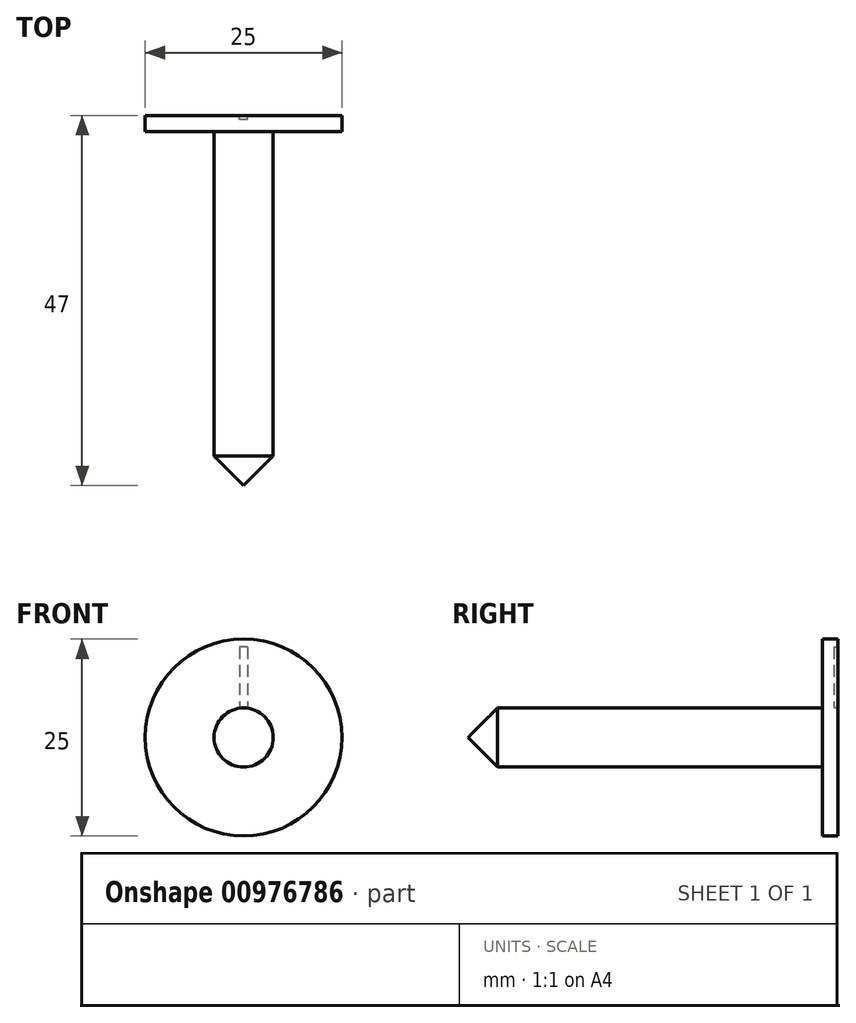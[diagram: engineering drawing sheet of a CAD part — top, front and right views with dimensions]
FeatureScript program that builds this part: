
annotation { "Feature Type Name" : "Feature", "Feature Type Description" : "" }
export const myFeature = defineFeature(function(context is Context, id is Id, definition is map)
    precondition{}
    {
        {
            var Q0;
            Q0=qCreatedBy(makeId("Front.planeOp"),FACE);
            var sketch = newSketch(context, id + "F0", { "sketchPlane" : qUnion([Q0])});
            skCircle(sketch, "E0", {"center": v(0, 0) * mm, "radius": 12.5 * mm});
            skSolve(sketch);
        }
        {
            var Q0;
            Q0 = qSketchRegion(id + "F0", true);
            extrude(context, id + "F1", {"entities" : qUnion([Q0]), "depth" : 2 * mm, "offsetDistance" : 25 * mm});
        }
        {
            var Q0;
            Q0=makeQuery(id+"F1.opExtrude","CAP_FACE",FACE,{"disambiguationData":[OSD([sQuery(id+"F0.wireOp",EDGE,"E0")])],"isStart":false});
            var sketch = newSketch(context, id + "F2", { "sketchPlane" : qUnion([Q0])});
            skCircle(sketch, "E1", {"center": v(0, 0) * mm, "radius": 3.75 * mm});
            skSolve(sketch);
        }
        {
            var Q0;
            Q0 = qSketchRegion(id + "F2", true);
            extrude(context, id + "F3", {"entities" : qUnion([Q0]), "operationType" : NewBodyOperationType.ADD, "depth" : 45 * mm, "offsetDistance" : 25 * mm});
        }
        {
            var Q0;
            Q0=makeQuery(id+"F3.opExtrude","CAP_EDGE",EDGE,{"disambiguationData":[OSD([sQuery(id+"F2.wireOp",EDGE,"E1")])],"isStart":false});
            chamfer(context, id + "F4", {"entities" : qUnion([Q0]), "width" : 3.75 * mm, "tangentPropagation" : true});
        }
        {
            var Q0;
            Q0=qCreatedBy(makeId("Right.planeOp"),FACE);
            var sketch = newSketch(context, id + "F5", { "sketchPlane" : qUnion([Q0])});
            skLineSegment(sketch, "E2", {"start": v(0, 0) * mm, "end": v(36.95, 0) * mm, "construction": true});
            skSolve(sketch);
        }
        {
            var Q0;
            Q0=qCreatedBy(makeId("Front.planeOp"),FACE);
            var sketch = newSketch(context, id + "F6", { "sketchPlane" : qUnion([Q0])});
            skLineSegment(sketch, "E3.top", {"start": v(0.5, 3.85) * mm, "end": v(-0.5, 3.85) * mm});
            skLineSegment(sketch, "E3.left", {"start": v(0.5, 11.49) * mm, "end": v(0.5, 3.85) * mm});
            skLineSegment(sketch, "E3.right", {"start": v(-0.5, 11.49) * mm, "end": v(-0.5, 3.85) * mm});
            skLineSegment(sketch, "E4", {"start": v(0, 0) * mm, "end": v(0, 13.73) * mm, "construction": true});
            skArc(sketch, "E5", {"start": v(0.5, 11.49) * mm, "mid": v(0, 11.5) * mm, "end": v(-0.5, 11.49) * mm});
            skSolve(sketch);
        }
        {
            var Q0;
            Q0 = qSketchRegion(id + "F6", true);
            extrude(context, id + "F7", {"entities" : qUnion([Q0]), "operationType" : NewBodyOperationType.REMOVE, "depth" : 0.5 * mm, "offsetDistance" : 25 * mm});
        }
    });
